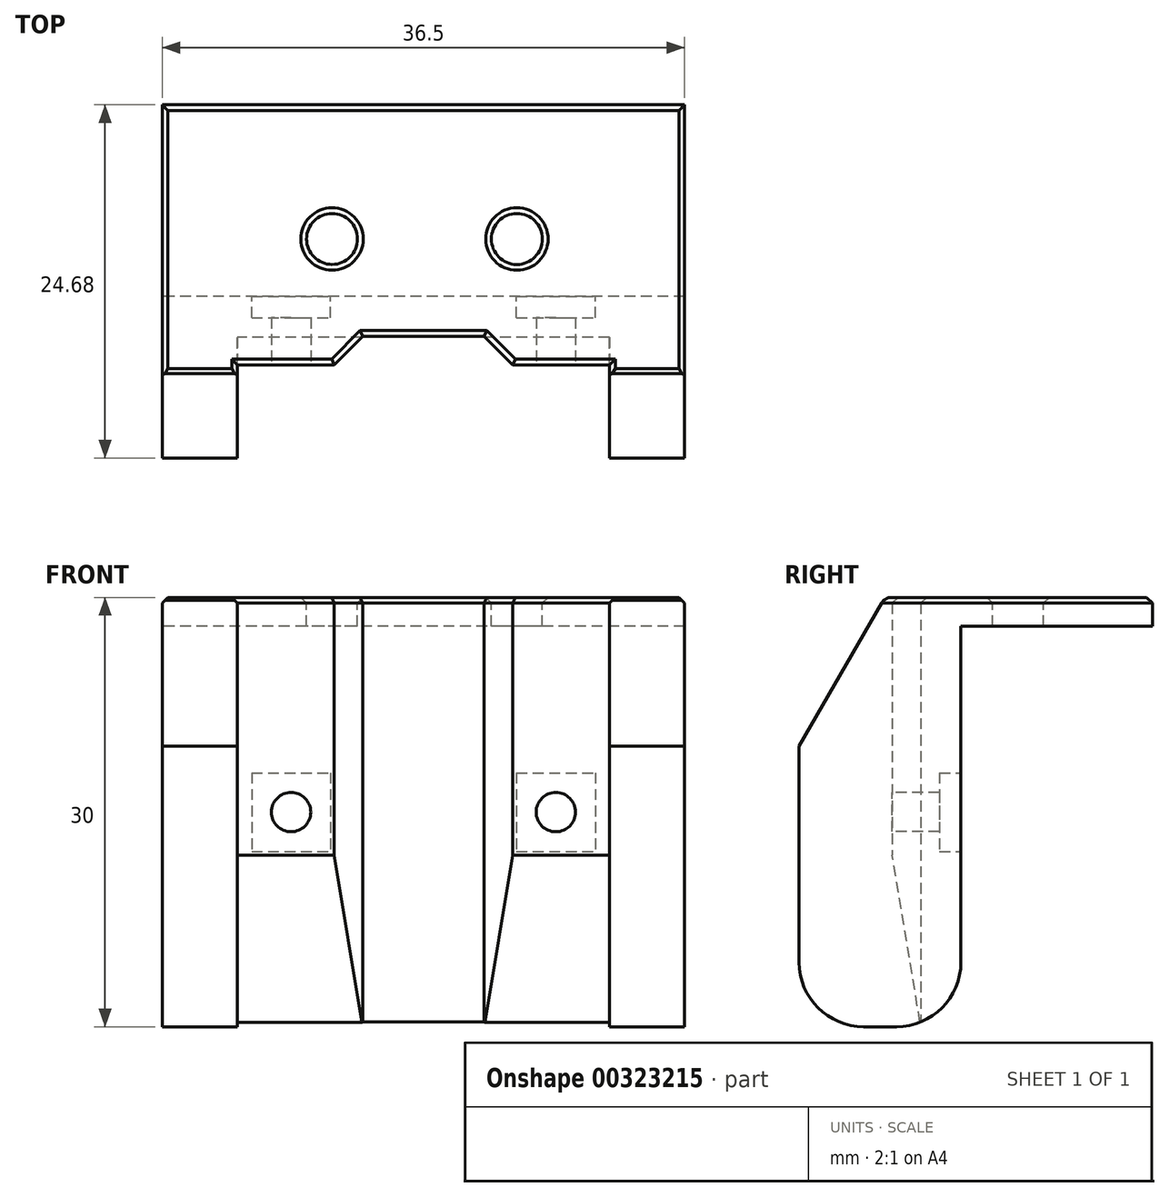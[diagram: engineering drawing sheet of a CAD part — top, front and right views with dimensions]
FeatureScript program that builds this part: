
annotation { "Feature Type Name" : "Feature", "Feature Type Description" : "" }
export const myFeature = defineFeature(function(context is Context, id is Id, definition is map)
    precondition{}
    {
        {
            var Q0;
            Q0=qCreatedBy(makeId("Right.planeOp"),FACE);
            var sketch = newSketch(context, id + "F0", { "sketchPlane" : qUnion([Q0])});
            skLineSegment(sketch, "E0", {"start": v(0, 0) * mm, "end": v(13.38, 0) * mm});
            skLineSegment(sketch, "E1", {"start": v(13.38, 0) * mm, "end": v(13.38, 2) * mm});
            skLineSegment(sketch, "E2", {"start": v(13.38, 2) * mm, "end": v(0, 2) * mm});
            skLineSegment(sketch, "E3", {"start": v(0, 2) * mm, "end": v(0, 0) * mm});
            skSolve(sketch);
        }
        {
            var Q0;
            Q0=makeQuery(id+"F0.imprint","IMPRINT",FACE,{"disambiguationData":[TD([[makeQuery(id+"F0.imprint","IMPRINT",EDGE,{"derivedFrom":sQuery(id+"F0.wireOp",EDGE,"E0")}),1.0]])]});
            extrude(context, id + "F1", {"entities" : qUnion([Q0]), "endBound" : BoundingType.SYMMETRIC, "depth" : 36.5 * mm});
        }
        {
            var Q0;
            Q0=makeQuery(id+"F1.opExtrude","SWEPT_FACE",FACE,{"disambiguationData":[OSD([sQuery(id+"F0.wireOp",EDGE,"E2")])]});
            var sketch = newSketch(context, id + "F2", { "sketchPlane" : qUnion([Q0])});
            skLineSegment(sketch, "E4", {"start": v(0, 13.38) * mm, "end": v(0, 0) * mm, "construction": true});
            skCircle(sketch, "E5", {"center": v(6.53, 4) * mm, "radius": 1.78 * mm});
            skCircle(sketch, "E6", {"center": v(-6.39, 4) * mm, "radius": 1.78 * mm});
            skPoint(sketch, "E7.center.orphan", {"position": v(13, 4) * mm});
            skLineSegment(sketch, "E8.trimOffspring", {"start": v(-8.17, 4) * mm, "end": v(8.3, 4) * mm, "construction": true});
            skPoint(sketch, "E9.orphan", {"position": v(-13, 4) * mm});
            skSolve(sketch);
        }
        {
            var Q0;
            Q0=qSketchRegion(id+"F2",true);
            extrude(context, id + "F3", {"entities" : qUnion([Q0]), "operationType" : NewBodyOperationType.REMOVE, "endBound" : BoundingType.UP_TO_NEXT, "oppositeDirection" : true, "depth" : 25 * mm});
        }
        {
            var Q0;
            Q0=qCreatedBy(makeId("Right.planeOp"),FACE);
            var sketch = newSketch(context, id + "F4", { "sketchPlane" : qUnion([Q0])});
            skLineSegment(sketch, "E10.bottom", {"start": v(0, 2) * mm, "end": v(-11.3, 2) * mm});
            skLineSegment(sketch, "E10.top", {"start": v(0, -28) * mm, "end": v(-11.3, -28) * mm});
            skLineSegment(sketch, "E10.left", {"start": v(0, 2) * mm, "end": v(0, -28) * mm});
            skLineSegment(sketch, "E10.right", {"start": v(-11.3, 2) * mm, "end": v(-11.3, -28) * mm});
            skSolve(sketch);
        }
        {
            var Q0;
            Q0=qSketchRegion(id+"F4",true);
            extrude(context, id + "F5", {"entities" : qUnion([Q0]), "operationType" : NewBodyOperationType.ADD, "endBound" : BoundingType.SYMMETRIC, "depth" : 36.5 * mm});
        }
        {
            var Q0;
            Q0=makeQuery(id+"F5.opExtrude","SWEPT_FACE",FACE,{"disambiguationData":[OSD([sQuery(id+"F4.wireOp",EDGE,"E10.top")])]});
            var sketch = newSketch(context, id + "F6", { "sketchPlane" : qUnion([Q0])});
            skLineSegment(sketch, "E11.bottom", {"start": v(-13, 11.3) * mm, "end": v(13, 11.3) * mm});
            skLineSegment(sketch, "E11.top", {"start": v(-13, 4.8) * mm, "end": v(13, 4.8) * mm});
            skLineSegment(sketch, "E11.left", {"start": v(-13, 11.3) * mm, "end": v(-13, 4.8) * mm});
            skLineSegment(sketch, "E11.right", {"start": v(13, 11.3) * mm, "end": v(13, 4.8) * mm});
            skLineSegment(sketch, "E12", {"start": v(0, 11.3) * mm, "end": v(0, 0) * mm, "construction": true});
            skSolve(sketch);
        }
        {
            var Q0;
            Q0=qSketchRegion(id+"F6",true);
            extrude(context, id + "F7", {"entities" : qUnion([Q0]), "operationType" : NewBodyOperationType.REMOVE, "endBound" : BoundingType.UP_TO_NEXT, "oppositeDirection" : true, "depth" : 25 * mm});
        }
        {
            var Q0;
            Q0=makeQuery(id+"F5.opExtrude","SWEPT_FACE",FACE,{"disambiguationData":[OSD([sQuery(id+"F4.wireOp",EDGE,"E10.top")])]});
            var sketch = newSketch(context, id + "F8", { "sketchPlane" : qUnion([Q0])});
            skLineSegment(sketch, "E13", {"start": v(0, 4.8) * mm, "end": v(0, 0) * mm, "construction": true});
            skLineSegment(sketch, "E14", {"start": v(-6.25, 4.8) * mm, "end": v(-4.25, 2.8) * mm});
            skLineSegment(sketch, "E15", {"start": v(-4.25, 2.8) * mm, "end": v(4.25, 2.8) * mm});
            skLineSegment(sketch, "E16", {"start": v(4.25, 2.8) * mm, "end": v(6.25, 4.8) * mm});
            skLineSegment(sketch, "E17", {"start": v(6.25, 4.8) * mm, "end": v(-6.25, 4.8) * mm});
            skSolve(sketch);
        }
        {
            var Q0;
            Q0=qSketchRegion(id+"F8",true);
            extrude(context, id + "F9", {"entities" : qUnion([Q0]), "operationType" : NewBodyOperationType.REMOVE, "endBound" : BoundingType.UP_TO_NEXT, "oppositeDirection" : true, "depth" : 25 * mm});
        }
        {
            var Q0;
            Q0=qCreatedBy(makeId("Right.planeOp"),FACE);
            var sketch = newSketch(context, id + "F10", { "sketchPlane" : qUnion([Q0])});
            skLineSegment(sketch, "E18", {"start": v(-2.8, -28) * mm, "end": v(-4.8, -16) * mm});
            skLineSegment(sketch, "E19", {"start": v(-4.8, -16) * mm, "end": v(-4.8, -28) * mm});
            skLineSegment(sketch, "E20", {"start": v(-4.8, -28) * mm, "end": v(-2.8, -28) * mm});
            skSolve(sketch);
        }
        {
            var Q0;
            Q0=qSketchRegion(id+"F10",true);
            var Q1;
            Q1=makeQuery(id+"F7.boolean.opBoolean","COPY",FACE,{"derivedFrom":makeQuery(id+"F7.opExtrude","SWEPT_FACE",FACE,{"disambiguationData":[OSD([sQuery(id+"F6.wireOp",EDGE,"E11.right")])]})});
            var Q2;
            Q2=makeQuery(id+"F7.boolean.opBoolean","COPY",FACE,{"derivedFrom":makeQuery(id+"F7.opExtrude","SWEPT_FACE",FACE,{"disambiguationData":[OSD([sQuery(id+"F6.wireOp",EDGE,"E11.left")])]})});
            extrude(context, id + "F11", {"entities" : qUnion([Q0]), "operationType" : NewBodyOperationType.REMOVE, "endBound" : BoundingType.UP_TO_SURFACE, "endBoundEntityFace" : qUnion([Q1]), "depth" : 25 * mm, "hasSecondDirection" : true, "secondDirectionBound" : SecondDirectionBoundingType.UP_TO_SURFACE, "secondDirectionOppositeDirection" : true, "secondDirectionBoundEntityFace" : qUnion([Q2]), "secondDirectionDepth" : 25 * mm});
        }
        {
            var Q0;
            Q0=makeQuery(id+"F9.boolean.opBoolean","SPLIT",FACE,{"disambiguationData":[TD([makeQuery(id+"F7.boolean.opBoolean","COPY",FACE,{"derivedFrom":makeQuery(id+"F7.opExtrude","SWEPT_FACE",FACE,{"disambiguationData":[OSD([sQuery(id+"F6.wireOp",EDGE,"E11.left")])]})})])],"derivedFrom":makeQuery(id+"F7.boolean.opBoolean","COPY",FACE,{"derivedFrom":makeQuery(id+"F7.opExtrude","SWEPT_FACE",FACE,{"disambiguationData":[OSD([sQuery(id+"F6.wireOp",EDGE,"E11.top")])]})})});
            var sketch = newSketch(context, id + "F12", { "sketchPlane" : qUnion([Q0])});
            skCircle(sketch, "E21", {"center": v(-9.25, -13) * mm, "radius": 1.38 * mm});
            skLineSegment(sketch, "E22", {"start": v(0, 2) * mm, "end": v(0, -28) * mm, "construction": true});
            skCircle(sketch, "E23.MirrorC", {"center": v(9.25, -13) * mm, "radius": 1.38 * mm});
            skSolve(sketch);
        }
        {
            var Q0;
            Q0=qSketchRegion(id+"F12",true);
            extrude(context, id + "F13", {"entities" : qUnion([Q0]), "operationType" : NewBodyOperationType.REMOVE, "endBound" : BoundingType.UP_TO_NEXT, "oppositeDirection" : true, "depth" : 25 * mm});
        }
        {
            var Q0;
            Q0=makeQuery(id+"F5.opExtrude","SWEPT_FACE",FACE,{"disambiguationData":[OSD([sQuery(id+"F4.wireOp",EDGE,"E10.left")])]});
            var sketch = newSketch(context, id + "F14", { "sketchPlane" : qUnion([Q0])});
            skLineSegment(sketch, "E24.bottom", {"start": v(-6.5, -10.25) * mm, "end": v(-12, -10.25) * mm});
            skLineSegment(sketch, "E24.top", {"start": v(-6.5, -15.75) * mm, "end": v(-12, -15.75) * mm});
            skLineSegment(sketch, "E24.left", {"start": v(-6.5, -10.25) * mm, "end": v(-6.5, -15.75) * mm});
            skLineSegment(sketch, "E24.right", {"start": v(-12, -10.25) * mm, "end": v(-12, -15.75) * mm});
            skPoint(sketch, "E24.middle", {"position": v(-9.25, -13) * mm});
            skLineSegment(sketch, "E25.bottom", {"start": v(12, -10.25) * mm, "end": v(6.5, -10.25) * mm});
            skLineSegment(sketch, "E25.top", {"start": v(12, -15.75) * mm, "end": v(6.5, -15.75) * mm});
            skLineSegment(sketch, "E25.left", {"start": v(12, -10.25) * mm, "end": v(12, -15.75) * mm});
            skLineSegment(sketch, "E25.right", {"start": v(6.5, -10.25) * mm, "end": v(6.5, -15.75) * mm});
            skPoint(sketch, "E25.middle", {"position": v(9.25, -13) * mm});
            skSolve(sketch);
        }
        {
            var Q0;
            Q0=qSketchRegion(id+"F14",true);
            extrude(context, id + "F15", {"entities" : qUnion([Q0]), "operationType" : NewBodyOperationType.REMOVE, "oppositeDirection" : true, "depth" : 1.5 * mm});
        }
        {
            var Q0;
            {var subQ0=sQuery(id+"F4.wireOp",EDGE,"E10.right");var subQ1=sQuery(id+"F4.wireOp",EDGE,"E10.top");Q0=makeQuery(id+"F7.boolean.opBoolean","SPLIT",EDGE,{"disambiguationData":[TD([makeQuery(id+"F7.opExtrude","SWEPT_FACE",FACE,{"disambiguationData":[OSD([sQuery(id+"F6.wireOp",EDGE,"E11.left")])]})])],"derivedFrom":makeQuery(id+"F5.opExtrude","SWEPT_EDGE",EDGE,{"disambiguationData":[OSD([subQ1,subQ0])]})});}
            var Q1;
            {var subQ0=sQuery(id+"F4.wireOp",EDGE,"E10.right");var subQ1=sQuery(id+"F4.wireOp",EDGE,"E10.top");Q1=makeQuery(id+"F7.boolean.opBoolean","SPLIT",EDGE,{"disambiguationData":[TD([makeQuery(id+"F7.opExtrude","SWEPT_FACE",FACE,{"disambiguationData":[OSD([sQuery(id+"F6.wireOp",EDGE,"E11.right")])]})])],"derivedFrom":makeQuery(id+"F5.opExtrude","SWEPT_EDGE",EDGE,{"disambiguationData":[OSD([subQ1,subQ0])]})});}
            var Q2;
            Q2=makeQuery(id+"F5.opExtrude","SWEPT_EDGE",EDGE,{"disambiguationData":[OSD([sQuery(id+"F4.wireOp",EDGE,"E10.top"),sQuery(id+"F4.wireOp",EDGE,"E10.left")])]});
            fillet(context, id + "F16", {"entities" : qUnion([Q0, Q1, Q2]), "radius" : 4.5 * mm, "tangentPropagation" : true, "allowEdgeOverflow" : false});
        }
        {
            var Q0;
            {var subQ0=sQuery(id+"F4.wireOp",EDGE,"E10.bottom");var subQ1=sQuery(id+"F4.wireOp",EDGE,"E10.right");Q0=makeQuery(id+"F7.boolean.opBoolean","SPLIT",EDGE,{"disambiguationData":[TD([makeQuery(id+"F7.opExtrude","SWEPT_FACE",FACE,{"disambiguationData":[OSD([sQuery(id+"F6.wireOp",EDGE,"E11.left")])]})])],"derivedFrom":makeQuery(id+"F5.opExtrude","SWEPT_EDGE",EDGE,{"disambiguationData":[OSD([subQ0,subQ1])]})});}
            var Q1;
            {var subQ0=sQuery(id+"F4.wireOp",EDGE,"E10.right");var subQ1=sQuery(id+"F4.wireOp",EDGE,"E10.bottom");Q1=makeQuery(id+"F7.boolean.opBoolean","SPLIT",EDGE,{"disambiguationData":[TD([makeQuery(id+"F7.opExtrude","SWEPT_FACE",FACE,{"disambiguationData":[OSD([sQuery(id+"F6.wireOp",EDGE,"E11.right")])]})])],"derivedFrom":makeQuery(id+"F5.opExtrude","SWEPT_EDGE",EDGE,{"disambiguationData":[OSD([subQ1,subQ0])]})});}
            chamfer(context, id + "F17", {"entities" : qUnion([Q0, Q1]), "chamferType" : ChamferType.OFFSET_ANGLE, "width" : 6 * mm, "oppositeDirection" : true, "angle" : 60 * degree, "tangentPropagation" : true});
        }
        {
            var Q0;
            Q0=makeQuery(id+"F5.boolean.opBoolean","MERGE",FACE,{"derivedFrom":[makeQuery(id+"F1.opExtrude","SWEPT_FACE",FACE,{"disambiguationData":[OSD([sQuery(id+"F0.wireOp",EDGE,"E2")])]}),makeQuery(id+"F5.opExtrude","SWEPT_FACE",FACE,{"disambiguationData":[OSD([sQuery(id+"F4.wireOp",EDGE,"E10.bottom")])]})]});
            chamfer(context, id + "F18", {"entities" : qUnion([Q0]), "width" : 0.4 * mm, "tangentPropagation" : true});
        }
    });
